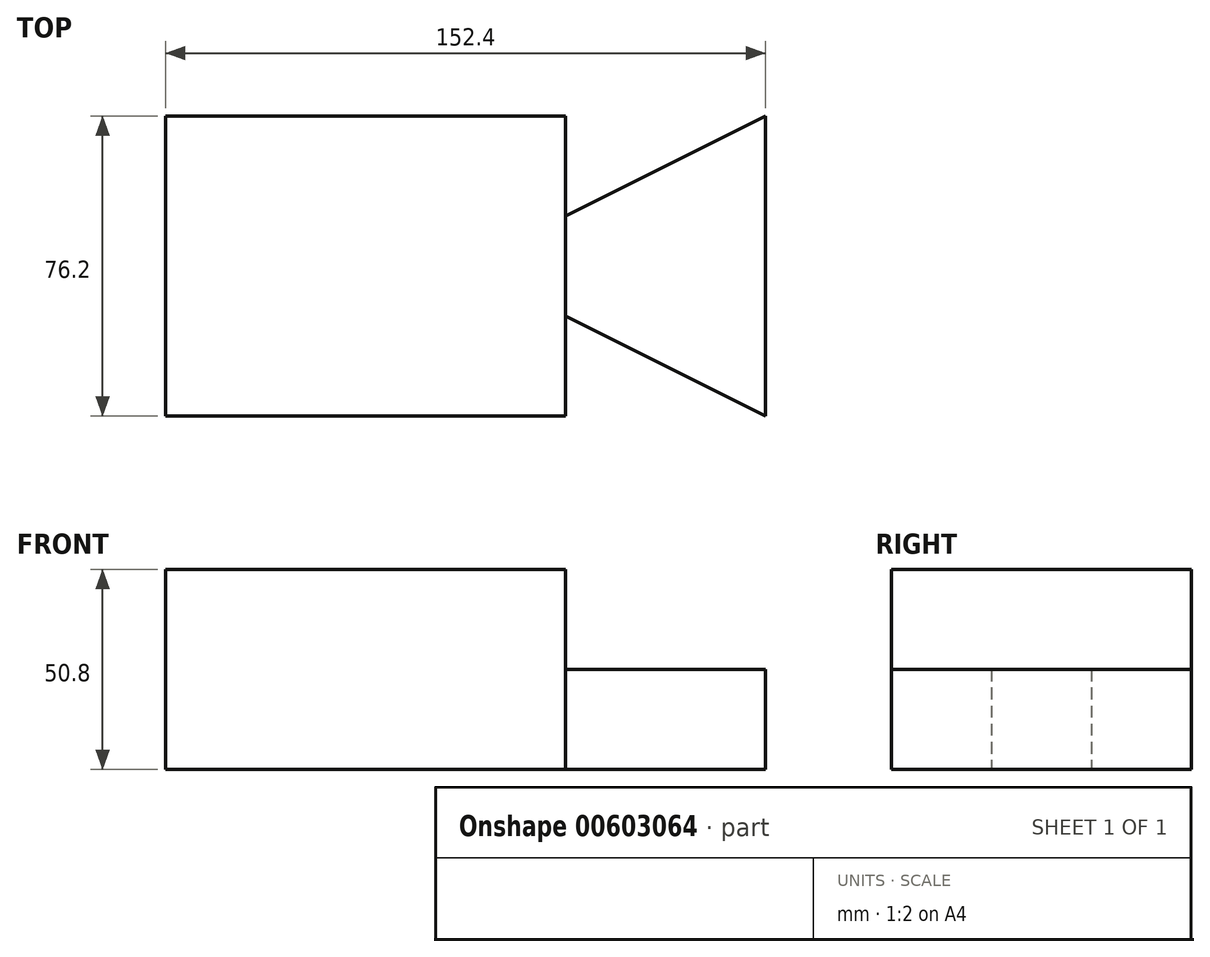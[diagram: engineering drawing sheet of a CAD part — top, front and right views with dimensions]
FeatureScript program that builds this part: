
annotation { "Feature Type Name" : "Feature", "Feature Type Description" : "" }
export const myFeature = defineFeature(function(context is Context, id is Id, definition is map)
    precondition{}
    {
        {
            var Q0;
            Q0=qCreatedBy(makeId("Top.planeOp"),FACE);
            var sketch = newSketch(context, id + "F0", { "sketchPlane" : qUnion([Q0])});
            skLineSegment(sketch, "E0.bottom", {"start": v(-89.87, 82.77) * mm, "end": v(11.73, 82.77) * mm});
            skLineSegment(sketch, "E0.top", {"start": v(-89.87, 6.57) * mm, "end": v(11.73, 6.57) * mm});
            skLineSegment(sketch, "E0.left", {"start": v(-89.87, 82.77) * mm, "end": v(-89.87, 6.57) * mm});
            skLineSegment(sketch, "E0.right", {"start": v(11.73, 82.77) * mm, "end": v(11.73, 6.57) * mm});
            skLineSegment(sketch, "E1", {"start": v(11.73, 82.77) * mm, "end": v(11.73, 57.37) * mm});
            skLineSegment(sketch, "E2", {"start": v(11.73, 31.97) * mm, "end": v(11.73, 6.57) * mm});
            skLineSegment(sketch, "E3", {"start": v(62.53, 82.77) * mm, "end": v(62.53, 6.57) * mm});
            skLineSegment(sketch, "E4", {"start": v(11.73, 57.37) * mm, "end": v(62.53, 82.77) * mm});
            skLineSegment(sketch, "E5", {"start": v(11.73, 31.97) * mm, "end": v(62.53, 6.57) * mm});
            skSolve(sketch);
        }
        {
            var Q0;
            Q0=makeQuery(id+"F0.imprint","IMPRINT",FACE,{"disambiguationData":[TD([[makeQuery(id+"F0.imprint","IMPRINT",EDGE,{"derivedFrom":sQuery(id+"F0.wireOp",EDGE,"E0.right")}),1.0]])]});
            extrude(context, id + "F1", {"entities" : qUnion([Q0]), "depth" : 25.4 * mm, "offsetDistance" : 25.4 * mm});
        }
        {
            var Q0;
            Q0=makeQuery(id+"F0.imprint","IMPRINT",FACE,{"disambiguationData":[TD([[makeQuery(id+"F0.imprint","IMPRINT",EDGE,{"derivedFrom":sQuery(id+"F0.wireOp",EDGE,"E0.bottom")}),-1.0]])]});
            extrude(context, id + "F2", {"entities" : qUnion([Q0]), "operationType" : NewBodyOperationType.ADD, "depth" : 50.8 * mm, "offsetDistance" : 25.4 * mm});
        }
    });
